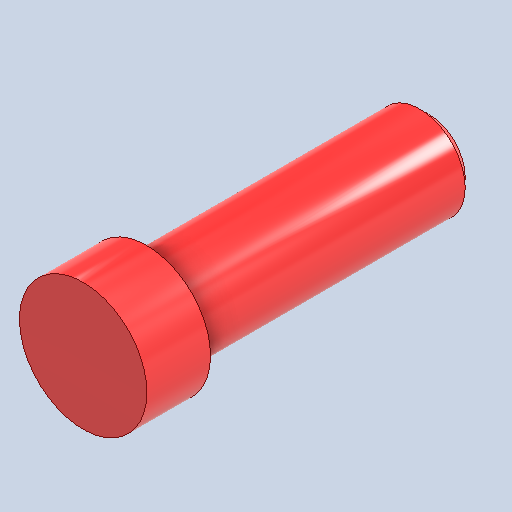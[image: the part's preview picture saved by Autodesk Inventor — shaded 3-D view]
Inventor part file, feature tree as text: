
AUTODESK INVENTOR PART (.ipt)
format: ipt  version: 2022 (Build 260153000, 153)  size: 122,880 bytes
history: native  units: in
note: dims shown in document units (in); Inventor stores cm internally (conversion verified against a paired STEP export)
features: other x3, sketch x2
ambient origin geometry x8: Origin, YZ Plane, XZ Plane, XY Plane, X Axis, Y Axis, Z Axis, Center Point
bodies: Solid1 (feature_tree)
feature tree (5):
  other  "bolt.ipt"
  other  "Solid1::bolt.ipt"
  other  "TaggingFeature1"
  sketch  "Sketch1"  dims[d0=0.3937in]
  sketch  "Sketch2"
